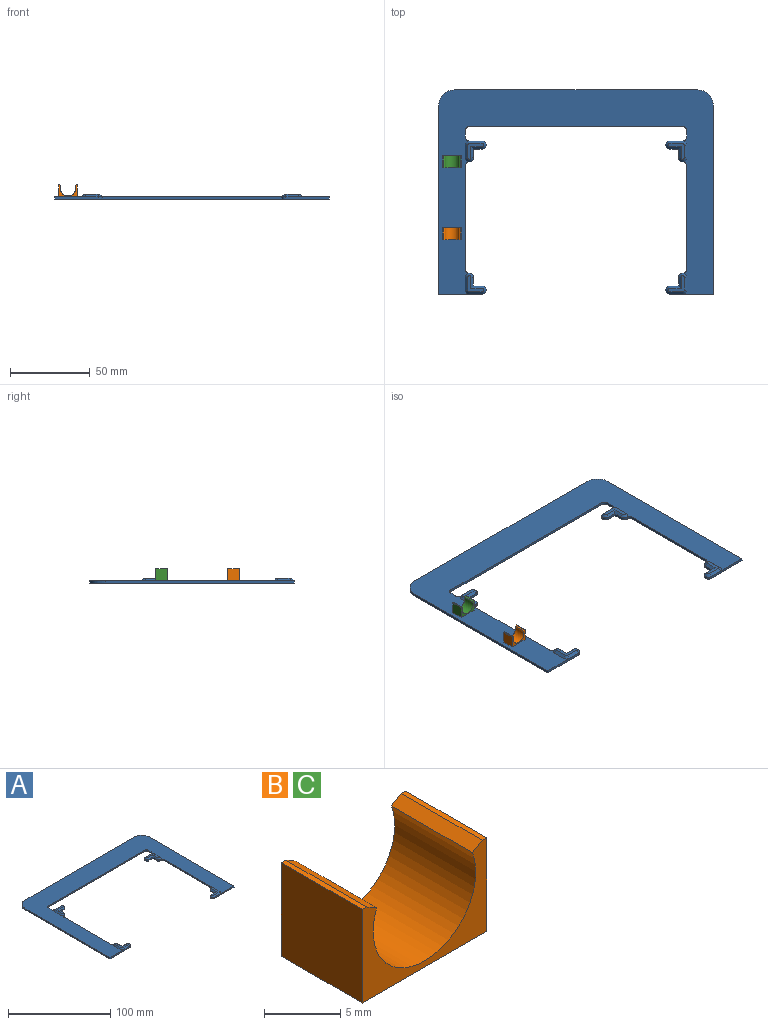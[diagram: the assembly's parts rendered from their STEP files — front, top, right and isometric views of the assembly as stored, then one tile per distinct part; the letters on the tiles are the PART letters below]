
ASSEMBLY  parts=3 mates=2
PART A: 72 faces, bbox 171.9x127.8x3 mm
  f0: plane 171.9x127.8mm, normal (0,0,1), area 7418.7mm2, adj f1,f2,f3,f4,f7,f11,f12,f13
  f1: plane 151.9x1.5mm, normal (0,1,0), area 227.9mm2, adj f0,f2,f22,f23
  f2: cylinder r=10mm len=10mm, axis (0,0,-1), area 23.6mm2, adj f0,f1,f3,f23
  f3: plane 117.8x1.5mm, normal (1,0,0), area 176.7mm2, adj f0,f2,f4,f23
  f4: plane 27.2x1.5mm, normal (0,-1,0), area 40.8mm2, adj f0,f3,f23,f34,f44
  f5: plane 5.5x1.5mm, normal (0,1,0), area 8.2mm2, adj f6,f23,f34,f48
  f6: plane 5.5x1.5mm, normal (-1,0,0), area 8.3mm2, adj f5,f23,f30,f50
  f7: plane 64.75x1.5mm, normal (-1,0,0), area 97.1mm2, adj f0,f23,f32,f38
  f8: plane 5.5x1.5mm, normal (-1,0,0), area 8.3mm2, adj f9,f23,f31,f52
  f9: plane 5.5x1.5mm, normal (0,-1,0), area 8.3mm2, adj f8,f23,f35,f53
  f10: plane 8x1.5mm, normal (0,1,0), area 12mm2, adj f23,f33,f35,f57
  f11: plane 4.15x1.5mm, normal (-1,0,0), area 6.2mm2, adj f0,f23,f33,f39
  f12: plane 133.5x1.5mm, normal (0,-1,0), area 200.3mm2, adj f0,f23,f39,f40
  f13: plane 4.15x1.5mm, normal (1,0,0), area 6.2mm2, adj f0,f23,f40,f41
  f14: plane 8x1.5mm, normal (0,1,0), area 12mm2, adj f23,f36,f41,f65
  f15: plane 5.5x1.5mm, normal (0,-1,0), area 8.3mm2, adj f16,f23,f36,f69
  f16: plane 5.5x1.5mm, normal (1,0,0), area 8.3mm2, adj f15,f23,f28,f71
  f17: plane 64.75x1.5mm, normal (1,0,0), area 97.1mm2, adj f0,f23,f42,f43
  f18: plane 5.5x1.5mm, normal (1,0,0), area 8.3mm2, adj f19,f23,f29,f64
  f19: plane 5.5x1.5mm, normal (0,1,0), area 8.2mm2, adj f18,f23,f37,f62
  f20: plane 27.2x1.5mm, normal (0,-1,0), area 40.8mm2, adj f0,f21,f23,f37,f58
  f21: plane 117.8x1.5mm, normal (-1,0,0), area 176.7mm2, adj f0,f20,f22,f23
  f22: cylinder r=10mm len=10mm, axis (0,0,-1), area 23.6mm2, adj f0,f1,f21,f23
  f23: plane 171.9x127.8mm, normal (0,0,-1), area 7811.9mm2, adj f1,f2,f3,f4,f5,f6,f7,f8
  f24: plane 10x10mm, normal (0,0,1), area 34.9mm2, adj f51,f52,f53,f54,f55,f56,f57
  f25: plane 10x10mm, normal (0,0,1), area 34.9mm2, adj f44,f45,f46,f47,f48,f49,f50
  f26: plane 10x10mm, normal (0,0,1), area 34.9mm2, adj f58,f59,f60,f61,f62,f63,f64
  f27: plane 10x10mm, normal (0,0,1), area 34.9mm2, adj f65,f66,f67,f68,f69,f70,f71
  f28: cylinder r=2.5mm len=2.5mm, axis (0,0,-1), area 5.9mm2, adj f16,f23,f42,f70
  f29: cylinder r=2.5mm len=2.5mm, axis (0,0,-1), area 5.9mm2, adj f18,f23,f43,f63
  f30: cylinder r=2.5mm len=2.5mm, axis (0,0,-1), area 5.9mm2, adj f6,f23,f38,f49
  f31: cylinder r=2.5mm len=2.5mm, axis (0,0,-1), area 5.9mm2, adj f8,f23,f32,f51
  f32: cylinder r=2.5mm len=2.5mm, axis (0,0,-1), area 5.9mm2, adj f0,f7,f23,f31
  f33: cylinder r=2.5mm len=2.5mm, axis (0,0,1), area 5.9mm2, adj f0,f10,f11,f23
  f34: cylinder r=2.5mm len=5mm, axis (0,0,-1), area 11.8mm2, adj f4,f5,f23,f46
  f35: cylinder r=2.5mm len=5mm, axis (0,0,-1), area 11.8mm2, adj f9,f10,f23,f55
  f36: cylinder r=2.5mm len=5mm, axis (0,0,1), area 11.8mm2, adj f14,f15,f23,f67
  f37: cylinder r=2.5mm len=5mm, axis (0,0,-1), area 11.8mm2, adj f19,f20,f23,f60
  f38: cylinder r=2.5mm len=2.5mm, axis (0,0,1), area 5.9mm2, adj f0,f7,f23,f30
  f39: cylinder r=2.5mm len=2.5mm, axis (0,0,-1), area 5.9mm2, adj f0,f11,f12,f23
  f40: cylinder r=2.5mm len=2.5mm, axis (0,0,1), area 5.9mm2, adj f0,f12,f13,f23
  f41: cylinder r=2.5mm len=2.5mm, axis (0,0,1), area 5.9mm2, adj f0,f13,f14,f23
  f42: cylinder r=2.5mm len=2.5mm, axis (0,0,1), area 5.9mm2, adj f0,f17,f23,f28
  f43: cylinder r=2.5mm len=2.5mm, axis (0,0,-1), area 5.9mm2, adj f0,f17,f23,f29
  f44: plane 8x1.5mm, normal (0,-0.71,0.71), area 17mm2, adj f4,f25,f45,f46
  f45: cone r=1mm half-angle=45deg, axis (0,0,-1), area 5.8mm2, adj f0,f25,f44,f47
  f46: cone r=1mm half-angle=45deg, axis (0,0,-1), area 11.7mm2, adj f25,f34,f44,f48
  f47: plane 8x1.5mm, normal (0.71,0,0.71), area 17mm2, adj f0,f25,f45,f49
  f48: plane 7x1.5mm, normal (0,0.71,0.71), area 13.3mm2, adj f5,f25,f46,f50
  f49: cone r=1mm half-angle=45deg, axis (0,0,-1), area 11.7mm2, adj f0,f25,f30,f47,f50
  f50: plane 7x1.5mm, normal (-0.71,0,0.71), area 13.3mm2, adj f6,f25,f48,f49
  f51: cone r=1mm half-angle=45deg, axis (0,0,-1), area 11.7mm2, adj f0,f24,f31,f52,f54
  f52: plane 7x1.5mm, normal (-0.71,0,0.71), area 13.3mm2, adj f8,f24,f51,f53
  f53: plane 7x1.5mm, normal (0,-0.71,0.71), area 13.3mm2, adj f9,f24,f52,f55
  f54: plane 8x1.5mm, normal (0.71,0,0.71), area 17mm2, adj f0,f24,f51,f56
  f55: cone r=1mm half-angle=45deg, axis (0,0,-1), area 11.7mm2, adj f24,f35,f53,f57
  f56: cone r=1mm half-angle=45deg, axis (0,0,-1), area 5.8mm2, adj f0,f24,f54,f57
  f57: plane 8x1.5mm, normal (0,0.71,0.71), area 17mm2, adj f10,f24,f55,f56
  f58: plane 8x1.5mm, normal (0,-0.71,0.71), area 17mm2, adj f20,f26,f59,f60
  f59: cone r=1mm half-angle=45deg, axis (0,0,-1), area 5.8mm2, adj f0,f26,f58,f61
  f60: cone r=1mm half-angle=45deg, axis (0,0,-1), area 11.7mm2, adj f26,f37,f58,f62
  f61: plane 8x1.5mm, normal (-0.71,0,0.71), area 17mm2, adj f0,f26,f59,f63
  f62: plane 7x1.5mm, normal (0,0.71,0.71), area 13.3mm2, adj f19,f26,f60,f64
  f63: cone r=1mm half-angle=45deg, axis (0,0,-1), area 11.7mm2, adj f0,f26,f29,f61,f64
  f64: plane 7x1.5mm, normal (0.71,0,0.71), area 13.3mm2, adj f18,f26,f62,f63
  f65: plane 8x1.5mm, normal (0,0.71,0.71), area 17mm2, adj f14,f27,f66,f67
  f66: cone r=1mm half-angle=45deg, axis (0,0,-1), area 5.8mm2, adj f0,f27,f65,f68
  f67: cone r=1mm half-angle=45deg, axis (0,0,-1), area 11.7mm2, adj f27,f36,f65,f69
  f68: plane 8x1.5mm, normal (-0.71,0,0.71), area 17mm2, adj f0,f27,f66,f70
  f69: plane 7x1.5mm, normal (0,-0.71,0.71), area 13.3mm2, adj f15,f27,f67,f71
  f70: cone r=1mm half-angle=45deg, axis (0,0,-1), area 11.7mm2, adj f0,f27,f28,f68,f71
  f71: plane 7x1.5mm, normal (0.71,0,0.71), area 13.3mm2, adj f16,f27,f69,f70
PART B: 10 faces, bbox 11.5x7.5x7.5 mm
  f0: plane 11.5x7.5mm, normal (0,0,-1), area 86.2mm2, adj f1,f7,f8,f9
  f1: plane 7.5x7.5mm, normal (-1,0,0), area 56.3mm2, adj f0,f2,f8,f9
  f2: plane 7.5x0.4mm, normal (0,0,1), area 3mm2, adj f1,f3,f8,f9
  f3: plane 7.5x0.92mm, normal (0.5,0,0.87), area 8mm2, adj f2,f4,f8,f9
  f4: cylinder r=4.75mm len=9.5mm, axis (0,-1,0), area 138.3mm2, adj f3,f5,f8,f9
  f5: plane 7.5x0.92mm, normal (-0.5,0,0.87), area 8mm2, adj f4,f6,f8,f9
  f6: plane 7.5x0.4mm, normal (0,0,1), area 3mm2, adj f5,f7,f8,f9
  f7: plane 7.5x7.5mm, normal (1,0,0), area 56.3mm2, adj f0,f6,f8,f9
  f8: plane 11.5x7.5mm, normal (0,1,0), area 29.6mm2, adj f0,f1,f2,f3,f4,f5,f6,f7
  f9: plane 11.5x7.5mm, normal (0,-1,0), area 29.6mm2, adj f0,f1,f2,f3,f4,f5,f6,f7
PART C: same geometry as B
PLACE A at identity fixed
PLACE B rot(axis=(-1,0,0),0deg) t=(8.84,-93.67,0.9)mm
PLACE C rot(axis=(-1,0,0),0deg) t=(8.84,-48.67,0.9)mm
MATE fastened C.f0 <-> A.f0  axis (0,0,-1) through (8.84,-44.92,0.9)mm
MATE fastened A.f0 <-> B.f0  axis (0,0,1) through (8.84,-79.92,0.9)mm
